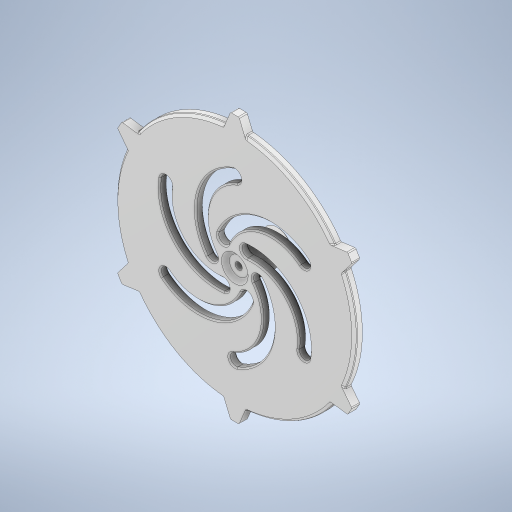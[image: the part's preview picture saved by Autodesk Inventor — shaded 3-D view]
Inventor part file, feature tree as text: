
AUTODESK INVENTOR PART (.ipt)
format: ipt  version: 2024 (Build 280153000, 153)  size: 709,632 bytes
history: native  units: mm
features: extrude x8, sketch x8, chamfer x5, plane x3, pattern_circular x3, fillet x2, projected_geometry x2, hole x1, split x1
ambient origin geometry x8: Origin, YZ Plane, XZ Plane, XY Plane, X Axis, Y Axis, Z Axis, Center Point
bodies: Solid1 (feature_tree), Solid2 (feature_tree), Solid3 (feature_tree)
feature tree (33):
  extrude  "Extrusion1"  Depth=14.0mm
  sketch  "Sketch2"  dims[d2=6.0mm d3=0.0mm d4=19.8mm]
  extrude  "Extrusion2"  Depth=6.0mm
  plane  "Work Plane1"
  extrude  "Extrusion3"  Depth=16.4mm TaperAngle=0.0deg
  plane  "Work Plane2"
  extrude  "Extrusion6"  Depth=1.0mm
  chamfer  "Chamfer8"  Distance=1.0mm Angle=45.0deg
  chamfer  "Chamfer4"  [1 undecoded]
  extrude  "Extrusion5"  Depth=1.0mm TaperAngle=360.0deg
  pattern_circular  "Circular Pattern1"  Angle=45.0deg  [1 undecoded]
  chamfer  "Chamfer6"  Distance=1.0mm Angle=45.0deg
  chamfer  "Chamfer7"  [1 undecoded]
  extrude  "Extrusion7"  Depth=10.0mm TaperAngle=0.0deg
  chamfer  "Chamfer9"  Distance=3.0mm Angle=45.0deg
  extrude  "Extrusion8"  Depth=6.0mm TaperAngle=0.0deg
  hole  "Hole1"  [1 undecoded]
  plane  "Work Plane3"
  split  "Split1"
  extrude  "Extrusion9"  Depth=1.0mm
  fillet  "Fillet2"  Radius=6.0mm
  pattern_circular  "Circular Pattern2"  [2 undecoded]
  fillet  "Fillet3"  Radius=20.0mm
  pattern_circular  "Circular Pattern3"  Angle=45.0deg  [1 undecoded]
  sketch  "Sketch1"  dims[d0=180.0mm d1=14.0mm]
  projected_geometry  "Projected Loop1"
  sketch  "Sketch4"  dims[d7=16.4mm d8=0.0mm d10=16.4mm d11=0.0mm]
  sketch  "Sketch5"  dims[d21=22.0mm d22=4.25mm d26=1.0mm d27=2.0mm d28=45.0deg]
  sketch  "Sketch6"  dims[d32=8.5mm]
  sketch  "Sketch7"  dims[d33=17.5mm]
  sketch  "Sketch8"  dims[d35=60.0mm]
  sketch  "Sketch9"  dims[d36=35.0mm d37=0.0mm d38=0.0mm d39=60.0mm d40=360.0deg d42=2.0mm d43=2.0mm d44=45.0deg d45=1.0mm d46=2.0mm d47=45.0deg d48=-3.0mm d49=10.0mm d50=0.0mm d51=3.0mm d52=2.0mm d53=45.0deg d54=6.0mm d55=0.0mm d56=1.0mm d57=2.0mm d58=45.0deg d59=8.25mm d60=6.0mm d61=0.0mm d62=5.3mm d63=6.0mm d64=4.0mm d65=2.0mm d66=90.0deg d67=8.0mm d68=20.594885mm d69=15.0mm d70=20.0mm d71=45.0deg d72=10.0mm d73=0.0mm d74=1.0mm d75=60.0mm d76=360.0deg d78=1.0mm d79=60.0mm d80=360.0deg d77=0.0mm]
  projected_geometry  "Project Cut Edges1"
note: 7 required parameter values undecoded (feature->parameter linkage not recoverable at this tier; creation-order binding heuristic only, values carry confidence <= 0.55)
